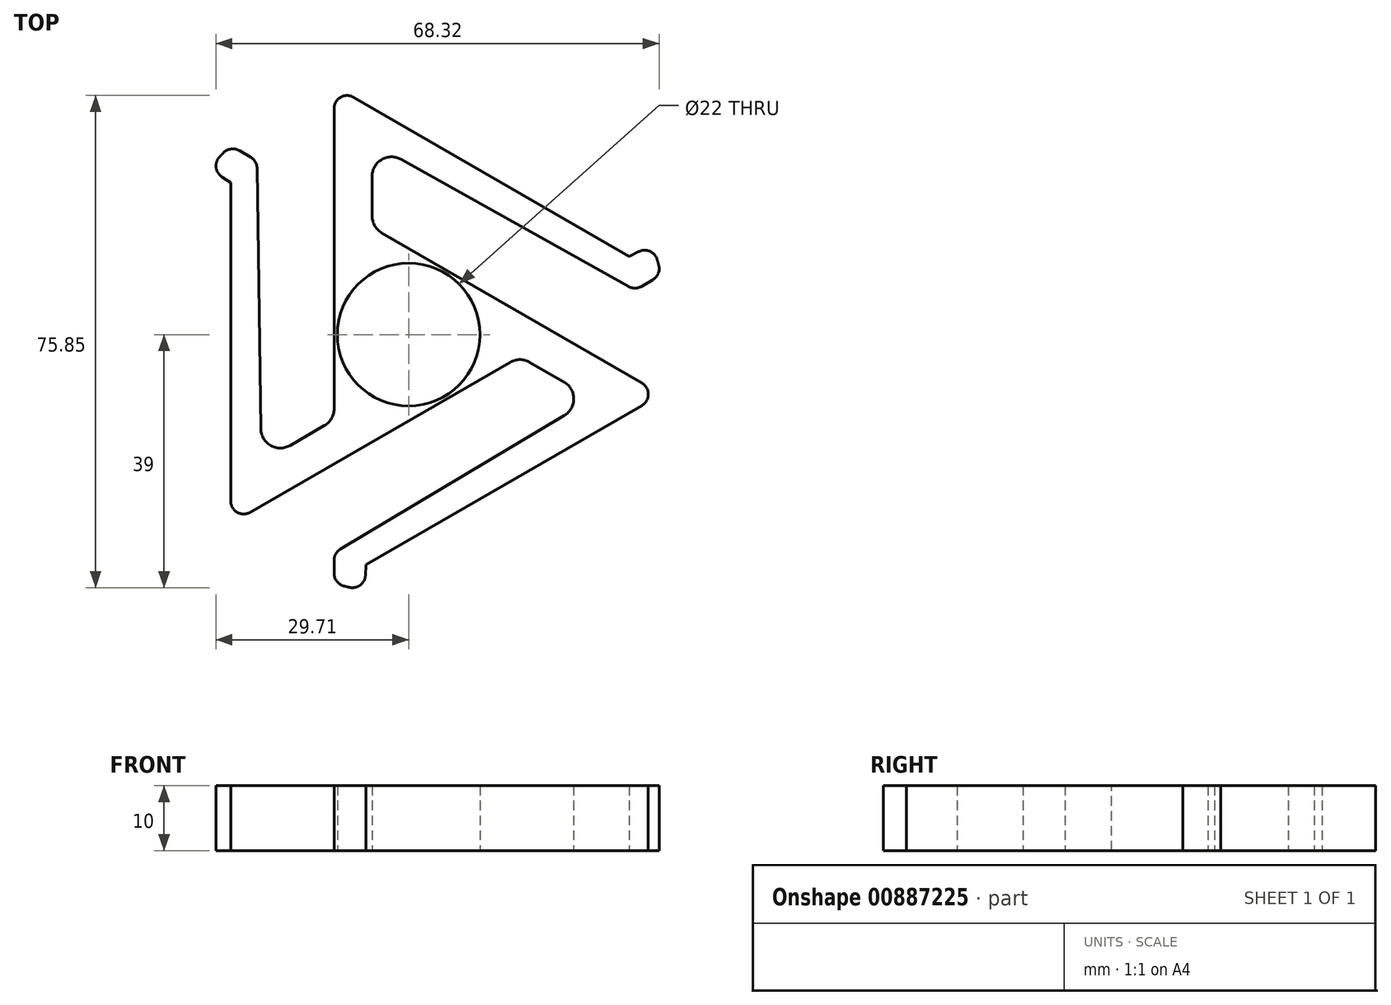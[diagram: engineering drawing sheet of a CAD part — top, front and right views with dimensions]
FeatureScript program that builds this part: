
annotation { "Feature Type Name" : "Feature", "Feature Type Description" : "" }
export const myFeature = defineFeature(function(context is Context, id is Id, definition is map)
    precondition{}
    {
        {
            var Q0;
            Q0=qCreatedBy(makeId("Top.planeOp"),FACE);
            var sketch = newSketch(context, id + "F0", { "sketchPlane" : qUnion([Q0])});
            skCircle(sketch, "E0", {"center": v(0, 0) * mm, "radius": 40 * mm});
            skCircle(sketch, "E1", {"center": v(0, 0) * mm, "radius": 11 * mm});
            skCircle(sketch, "E2.cCircle", {"center": v(0, 0) * mm, "radius": 23 * mm, "construction": true});
            skLineSegment(sketch, "E2.0", {"start": v(23, 0) * mm, "end": v(-11.5, -19.92) * mm});
            skLineSegment(sketch, "E2.1", {"start": v(-11.5, -19.92) * mm, "end": v(-11.5, 19.92) * mm});
            skLineSegment(sketch, "E2.2", {"start": v(-11.5, 19.92) * mm, "end": v(23, 0) * mm});
            skLineSegment(sketch, "E3", {"start": v(-11.5, 19.92) * mm, "end": v(-11.5, 38.31) * mm});
            skLineSegment(sketch, "E4", {"start": v(-11.5, 38.31) * mm, "end": v(54.86, 0) * mm});
            skLineSegment(sketch, "E5", {"start": v(23, 0) * mm, "end": v(38.93, 9.2) * mm});
            skLineSegment(sketch, "E6", {"start": v(-11.5, 32.77) * mm, "end": v(34.88, 6.86) * mm});
            skLineSegment(sketch, "E7", {"start": v(-5.64, 34.93) * mm, "end": v(-5.64, 16.54) * mm});
            skLineSegment(sketch, "E8", {"start": v(34, 12.04) * mm, "end": v(37.53, 13.83) * mm});
            skLineSegment(sketch, "E9.1.0", {"start": v(-27.43, 23.42) * mm, "end": v(-30.74, 25.59) * mm});
            skLineSegment(sketch, "E9.1.1", {"start": v(-11.5, 19.92) * mm, "end": v(-27.43, 29.11) * mm});
            skLineSegment(sketch, "E9.1.2", {"start": v(-27.43, -29.11) * mm, "end": v(-27.43, 47.5) * mm});
            skLineSegment(sketch, "E9.1.3", {"start": v(-22.63, -26.34) * mm, "end": v(-23.38, 26.78) * mm});
            skLineSegment(sketch, "E9.1.4", {"start": v(-27.43, -22.35) * mm, "end": v(-11.5, -13.16) * mm});
            skLineSegment(sketch, "E9.1.5", {"start": v(-11.5, -19.92) * mm, "end": v(-27.43, -29.11) * mm});
            skLineSegment(sketch, "E9.2.0", {"start": v(-6.57, -35.47) * mm, "end": v(-6.79, -39.42) * mm});
            skLineSegment(sketch, "E9.2.1", {"start": v(-11.5, -19.92) * mm, "end": v(-11.5, -38.31) * mm});
            skLineSegment(sketch, "E9.2.2", {"start": v(38.93, -9.2) * mm, "end": v(-27.43, -47.5) * mm});
            skLineSegment(sketch, "E9.2.3", {"start": v(34.13, -6.42) * mm, "end": v(-11.5, -33.64) * mm});
            skLineSegment(sketch, "E9.2.4", {"start": v(33.07, -12.58) * mm, "end": v(17.14, -3.38) * mm});
            skLineSegment(sketch, "E9.2.5", {"start": v(23, 0) * mm, "end": v(38.93, -9.2) * mm});
            skSolve(sketch);
        }
        {
            var Q0;
            {var subQ3=sQuery(id+"F0.wireOp",EDGE,"E8");Q0=makeQuery(id+"F0.imprint","IMPRINT",FACE,{"disambiguationData":[TD([[makeQuery(id+"F0.imprint","IMPRINT",EDGE,{"derivedFrom":subQ3}),-1.0]])]});}
            var Q1;
            {var subQ0=sQuery(id+"F0.wireOp",EDGE,"E9.1.0");Q1=makeQuery(id+"F0.imprint","IMPRINT",FACE,{"disambiguationData":[TD([[makeQuery(id+"F0.imprint","IMPRINT",EDGE,{"derivedFrom":subQ0}),-1.0]])]});}
            var Q2;
            {var subQ0=sQuery(id+"F0.wireOp",EDGE,"E9.2.0");Q2=makeQuery(id+"F0.imprint","IMPRINT",FACE,{"disambiguationData":[TD([[makeQuery(id+"F0.imprint","IMPRINT",EDGE,{"derivedFrom":subQ0}),-1.0]])]});}
            var Q3;
            {var subQ1=sQuery(id+"F0.wireOp",EDGE,"E3");var subQ3=sQuery(id+"F0.wireOp",EDGE,"E6");var subQ4=makeQuery(id+"F0.imprint","INTERSECT",VERTEX,{"derivedFrom":[subQ1,subQ3]});Q3=makeQuery(id+"F0.imprint","IMPRINT",FACE,{"disambiguationData":[TD([[makeQuery(id+"F0.imprint","IMPRINT",EDGE,{"disambiguationData":[TD([[subQ4,-1.0]])],"derivedFrom":subQ3}),1.0]])]});}
            var Q4;
            {var subQ0=sQuery(id+"F0.wireOp",EDGE,"E9.1.5");var subQ5=sQuery(id+"F0.wireOp",EDGE,"E9.1.3");var subQ7=makeQuery(id+"F0.imprint","INTERSECT",VERTEX,{"derivedFrom":[subQ5,subQ0]});Q4=makeQuery(id+"F0.imprint","IMPRINT",FACE,{"disambiguationData":[TD([[makeQuery(id+"F0.imprint","IMPRINT",EDGE,{"disambiguationData":[TD([[subQ7,-1.0]])],"derivedFrom":subQ5}),1.0]])]});}
            var Q5;
            {var subQ0=sQuery(id+"F0.wireOp",EDGE,"E9.2.5");var subQ5=sQuery(id+"F0.wireOp",EDGE,"E9.2.3");var subQ7=makeQuery(id+"F0.imprint","INTERSECT",VERTEX,{"derivedFrom":[subQ5,subQ0]});Q5=makeQuery(id+"F0.imprint","IMPRINT",FACE,{"disambiguationData":[TD([[makeQuery(id+"F0.imprint","IMPRINT",EDGE,{"disambiguationData":[TD([[subQ7,-1.0]])],"derivedFrom":subQ5}),1.0]])]});}
            var Q6;
            {var subQ1=sQuery(id+"F0.wireOp",EDGE,"E4");var subQ6=sQuery(id+"F0.wireOp",EDGE,"E7");var subQ8=makeQuery(id+"F0.imprint","INTERSECT",VERTEX,{"derivedFrom":[subQ1,subQ6]});Q6=makeQuery(id+"F0.imprint","IMPRINT",FACE,{"disambiguationData":[TD([[makeQuery(id+"F0.imprint","IMPRINT",EDGE,{"disambiguationData":[TD([[subQ8,-1.0]])],"derivedFrom":subQ1}),-1.0]])]});}
            var Q7;
            {var subQ0=sQuery(id+"F0.wireOp",EDGE,"E9.1.2");var subQ1=makeQuery(id+"F0.imprint","INTERSECT",VERTEX,{"derivedFrom":[sQuery(id+"F0.wireOp",EDGE,"E9.1.0"),subQ0]});Q7=makeQuery(id+"F0.imprint","IMPRINT",FACE,{"disambiguationData":[TD([[makeQuery(id+"F0.imprint","IMPRINT",EDGE,{"disambiguationData":[TD([[subQ1,1.0]])],"derivedFrom":subQ0}),-1.0]])]});}
            var Q8;
            {var subQ0=sQuery(id+"F0.wireOp",EDGE,"E9.2.2");var subQ1=makeQuery(id+"F0.imprint","INTERSECT",VERTEX,{"derivedFrom":[sQuery(id+"F0.wireOp",EDGE,"E9.2.0"),subQ0]});Q8=makeQuery(id+"F0.imprint","IMPRINT",FACE,{"disambiguationData":[TD([[makeQuery(id+"F0.imprint","IMPRINT",EDGE,{"disambiguationData":[TD([[subQ1,1.0]])],"derivedFrom":subQ0}),-1.0]])]});}
            var Q9;
            Q9=makeQuery(id+"F0.imprint","IMPRINT",FACE,{"disambiguationData":[TD([[makeQuery(id+"F0.imprint","IMPRINT",EDGE,{"derivedFrom":sQuery(id+"F0.wireOp",EDGE,"E1")}),-1.0]])]});
            var Q10;
            {var subQ0=sQuery(id+"F0.wireOp",EDGE,"E3");var subQ5=sQuery(id+"F0.wireOp",EDGE,"E6");var subQ6=makeQuery(id+"F0.imprint","INTERSECT",VERTEX,{"derivedFrom":[subQ0,subQ5]});Q10=makeQuery(id+"F0.imprint","IMPRINT",FACE,{"disambiguationData":[TD([[makeQuery(id+"F0.imprint","IMPRINT",EDGE,{"disambiguationData":[TD([[subQ6,-1.0]])],"derivedFrom":subQ5}),-1.0]])]});}
            var Q11;
            {var subQ0=sQuery(id+"F0.wireOp",EDGE,"E9.1.5");var subQ5=sQuery(id+"F0.wireOp",EDGE,"E9.1.3");var subQ7=makeQuery(id+"F0.imprint","INTERSECT",VERTEX,{"derivedFrom":[subQ5,subQ0]});Q11=makeQuery(id+"F0.imprint","IMPRINT",FACE,{"disambiguationData":[TD([[makeQuery(id+"F0.imprint","IMPRINT",EDGE,{"disambiguationData":[TD([[subQ7,-1.0]])],"derivedFrom":subQ5}),-1.0]])]});}
            var Q12;
            {var subQ0=sQuery(id+"F0.wireOp",EDGE,"E9.2.5");var subQ5=sQuery(id+"F0.wireOp",EDGE,"E9.2.3");var subQ6=makeQuery(id+"F0.imprint","INTERSECT",VERTEX,{"derivedFrom":[subQ5,subQ0]});Q12=makeQuery(id+"F0.imprint","IMPRINT",FACE,{"disambiguationData":[TD([[makeQuery(id+"F0.imprint","IMPRINT",EDGE,{"disambiguationData":[TD([[subQ6,-1.0]])],"derivedFrom":subQ5}),-1.0]])]});}
            extrude(context, id + "F1", {"entities" : qUnion([Q0, Q1, Q2, Q3, Q4, Q5, Q6, Q7, Q8, Q9, Q10, Q11, Q12]), "depth" : 10 * mm, "offsetDistance" : 25 * mm});
        }
        {
            var Q0;
            Q0=makeQuery(id+"F1.opExtrude","SWEPT_EDGE",EDGE,{"disambiguationData":[OSD([sQuery(id+"F0.wireOp",EDGE,"E0"),sQuery(id+"F0.wireOp",EDGE,"E8")])]});
            var Q1;
            Q1=makeQuery(id+"F1.opExtrude","SWEPT_EDGE",EDGE,{"disambiguationData":[OSD([sQuery(id+"F0.wireOp",EDGE,"E0"),sQuery(id+"F0.wireOp",EDGE,"E3"),sQuery(id+"F0.wireOp",EDGE,"E4")])]});
            var Q2;
            Q2=makeQuery(id+"F1.opExtrude","SWEPT_EDGE",EDGE,{"disambiguationData":[OSD([sQuery(id+"F0.wireOp",EDGE,"E0"),sQuery(id+"F0.wireOp",EDGE,"E9.2.2"),sQuery(id+"F0.wireOp",EDGE,"E9.2.5")])]});
            var Q3;
            Q3=makeQuery(id+"F1.opExtrude","SWEPT_EDGE",EDGE,{"disambiguationData":[OSD([sQuery(id+"F0.wireOp",EDGE,"E0"),sQuery(id+"F0.wireOp",EDGE,"E4"),sQuery(id+"F0.wireOp",EDGE,"E5")])]});
            var Q4;
            Q4=makeQuery(id+"F1.opExtrude","SWEPT_EDGE",EDGE,{"disambiguationData":[OSD([sQuery(id+"F0.wireOp",EDGE,"E5"),sQuery(id+"F0.wireOp",EDGE,"E6")])]});
            var Q5;
            Q5=makeQuery(id+"F1.opExtrude","SWEPT_EDGE",EDGE,{"disambiguationData":[OSD([sQuery(id+"F0.wireOp",EDGE,"E0"),sQuery(id+"F0.wireOp",EDGE,"E9.2.0")])]});
            var Q6;
            Q6=makeQuery(id+"F1.opExtrude","SWEPT_EDGE",EDGE,{"disambiguationData":[OSD([sQuery(id+"F0.wireOp",EDGE,"E9.2.1"),sQuery(id+"F0.wireOp",EDGE,"E9.2.3")])]});
            var Q7;
            Q7=makeQuery(id+"F1.opExtrude","SWEPT_EDGE",EDGE,{"disambiguationData":[OSD([sQuery(id+"F0.wireOp",EDGE,"E0"),sQuery(id+"F0.wireOp",EDGE,"E9.2.1"),sQuery(id+"F0.wireOp",EDGE,"E9.2.2")])]});
            var Q8;
            Q8=makeQuery(id+"F1.opExtrude","SWEPT_EDGE",EDGE,{"disambiguationData":[OSD([sQuery(id+"F0.wireOp",EDGE,"E0"),sQuery(id+"F0.wireOp",EDGE,"E9.1.2"),sQuery(id+"F0.wireOp",EDGE,"E9.1.5")])]});
            var Q9;
            Q9=makeQuery(id+"F1.opExtrude","SWEPT_EDGE",EDGE,{"disambiguationData":[OSD([sQuery(id+"F0.wireOp",EDGE,"E0"),sQuery(id+"F0.wireOp",EDGE,"E9.1.0")])]});
            var Q10;
            Q10=makeQuery(id+"F1.opExtrude","SWEPT_EDGE",EDGE,{"disambiguationData":[OSD([sQuery(id+"F0.wireOp",EDGE,"E0"),sQuery(id+"F0.wireOp",EDGE,"E9.1.1"),sQuery(id+"F0.wireOp",EDGE,"E9.1.2")])]});
            var Q11;
            Q11=makeQuery(id+"F1.opExtrude","SWEPT_EDGE",EDGE,{"disambiguationData":[OSD([sQuery(id+"F0.wireOp",EDGE,"E9.1.1"),sQuery(id+"F0.wireOp",EDGE,"E9.1.3")])]});
            fillet(context, id + "F2", {"entities" : qUnion([Q0, Q1, Q2, Q3, Q4, Q5, Q6, Q7, Q8, Q9, Q10, Q11]), "radius" : 2 * mm, "tangentPropagation" : true, "allowEdgeOverflow" : false});
        }
        {
            var Q0;
            Q0=makeQuery(id+"F1.opExtrude","SWEPT_EDGE",EDGE,{"disambiguationData":[OSD([sQuery(id+"F0.wireOp",EDGE,"E9.2.3"),sQuery(id+"F0.wireOp",EDGE,"E9.2.4")])]});
            var Q1;
            Q1=makeQuery(id+"F1.opExtrude","SWEPT_EDGE",EDGE,{"disambiguationData":[OSD([sQuery(id+"F0.wireOp",EDGE,"E2.0"),sQuery(id+"F0.wireOp",EDGE,"E9.2.4")])]});
            var Q2;
            Q2=makeQuery(id+"F1.opExtrude","SWEPT_EDGE",EDGE,{"disambiguationData":[OSD([sQuery(id+"F0.wireOp",EDGE,"E2.2"),sQuery(id+"F0.wireOp",EDGE,"E7")])]});
            var Q3;
            Q3=makeQuery(id+"F1.opExtrude","SWEPT_EDGE",EDGE,{"disambiguationData":[OSD([sQuery(id+"F0.wireOp",EDGE,"E6"),sQuery(id+"F0.wireOp",EDGE,"E7")])]});
            var Q4;
            Q4=makeQuery(id+"F1.opExtrude","SWEPT_EDGE",EDGE,{"disambiguationData":[OSD([sQuery(id+"F0.wireOp",EDGE,"E2.1"),sQuery(id+"F0.wireOp",EDGE,"E9.1.4")])]});
            var Q5;
            Q5=makeQuery(id+"F1.opExtrude","SWEPT_EDGE",EDGE,{"disambiguationData":[OSD([sQuery(id+"F0.wireOp",EDGE,"E9.1.3"),sQuery(id+"F0.wireOp",EDGE,"E9.1.4")])]});
            fillet(context, id + "F3", {"entities" : qUnion([Q0, Q1, Q2, Q3, Q4, Q5]), "radius" : 3 * mm, "tangentPropagation" : true, "allowEdgeOverflow" : false});
        }
    });
